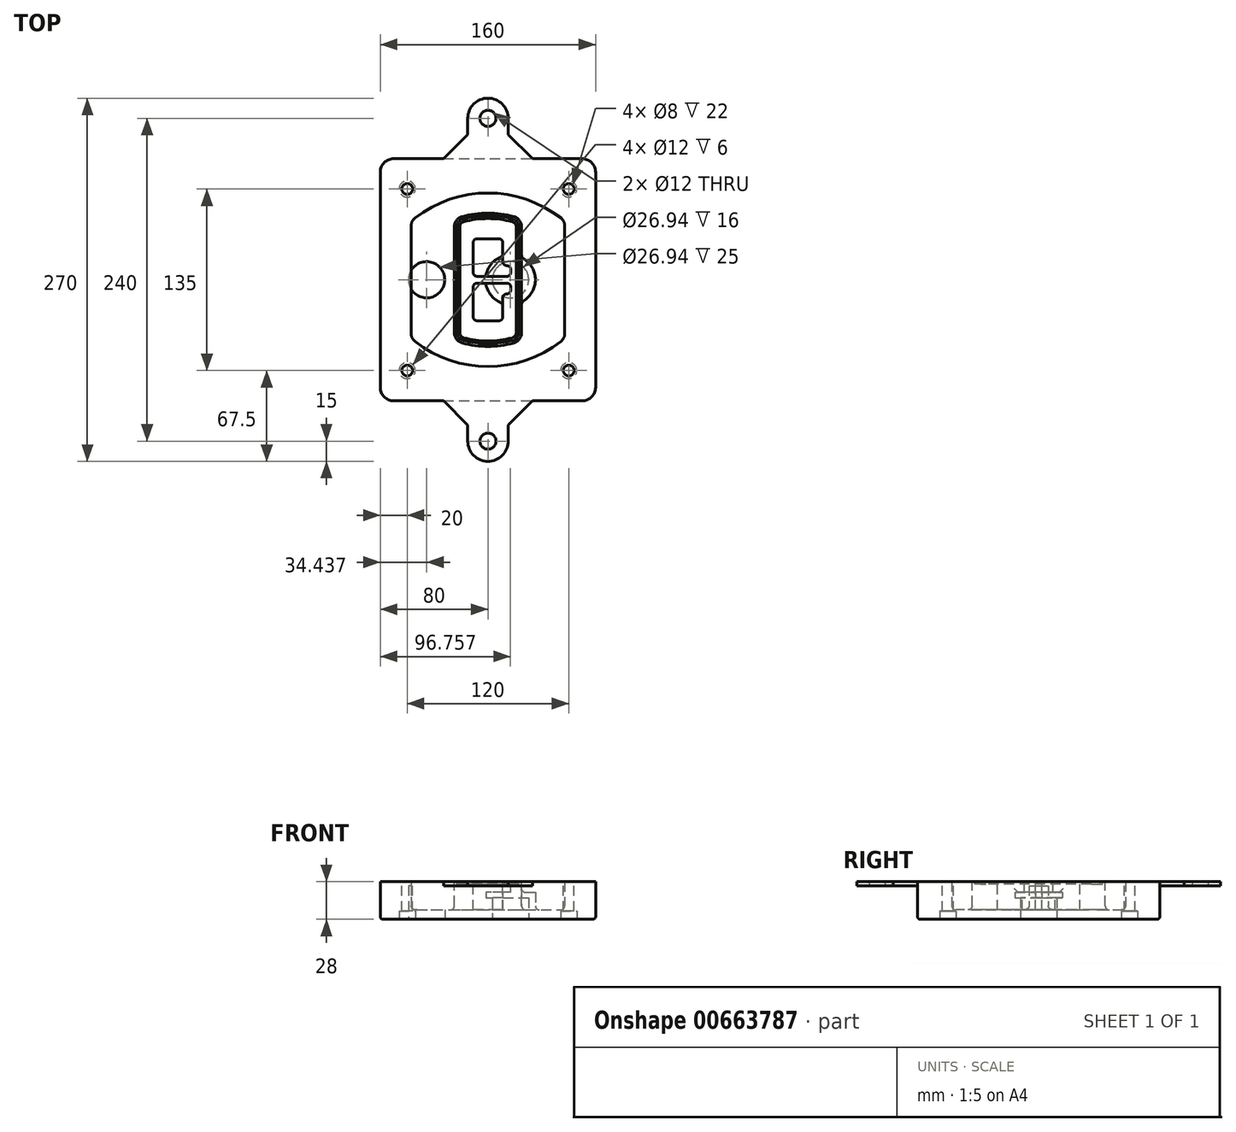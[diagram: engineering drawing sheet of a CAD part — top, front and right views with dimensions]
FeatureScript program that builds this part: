
annotation { "Feature Type Name" : "Feature", "Feature Type Description" : "" }
export const myFeature = defineFeature(function(context is Context, id is Id, definition is map)
    precondition{}
    {
        {
            var Q0;
            Q0=qCreatedBy(makeId("Top.planeOp"),FACE);
            var sketch = newSketch(context, id + "F0", { "sketchPlane" : qUnion([Q0])});
            skPoint(sketch, "E0.rect.middle", {"position": v(0, 0) * mm});
            skLineSegment(sketch, "E1.bottom", {"start": v(-70, -90) * mm, "end": v(70, -90) * mm});
            skLineSegment(sketch, "E1.top", {"start": v(-70, 90) * mm, "end": v(70, 90) * mm});
            skLineSegment(sketch, "E1.left", {"start": v(-80, -80) * mm, "end": v(-80, 80) * mm});
            skLineSegment(sketch, "E1.right", {"start": v(80, -80) * mm, "end": v(80, 80) * mm});
            skLineSegment(sketch, "E2", {"start": v(-80, 90) * mm, "end": v(80, -90) * mm, "construction": true});
            skLineSegment(sketch, "E3", {"start": v(80, 90) * mm, "end": v(-80, -90) * mm, "construction": true});
            skCircle(sketch, "E4", {"center": v(-60, 67.5) * mm, "radius": 4 * mm});
            skCircle(sketch, "E5", {"center": v(60, 67.5) * mm, "radius": 4 * mm});
            skCircle(sketch, "E6", {"center": v(60, -67.5) * mm, "radius": 4 * mm});
            skCircle(sketch, "E7", {"center": v(-60, -67.5) * mm, "radius": 4 * mm});
            skLineSegment(sketch, "E8", {"start": v(-60, 67.5) * mm, "end": v(60, 67.5) * mm, "construction": true});
            skLineSegment(sketch, "E9", {"start": v(60, 67.5) * mm, "end": v(60, -67.5) * mm, "construction": true});
            skLineSegment(sketch, "E10", {"start": v(60, -67.5) * mm, "end": v(-60, -67.5) * mm, "construction": true});
            skLineSegment(sketch, "E11", {"start": v(-60, -67.5) * mm, "end": v(-60, 67.5) * mm, "construction": true});
            skLineSegment(sketch, "E12", {"start": v(-60, 40.3) * mm, "end": v(-60, -40.3) * mm});
            skLineSegment(sketch, "E13", {"start": v(60, 40.3) * mm, "end": v(60, -40.3) * mm});
            skArc(sketch, "E14", {"start": v(56.15, 48.18) * mm, "mid": v(0, 67.5) * mm, "end": v(-56.15, 48.18) * mm});
            skArc(sketch, "E15", {"start": v(-56.15, -48.18) * mm, "mid": v(0, -67.5) * mm, "end": v(56.15, -48.18) * mm});
            skLineSegment(sketch, "E16", {"start": v(-60, 0) * mm, "end": v(60, 0) * mm, "construction": true});
            skPoint(sketch, "E17.visualSharp", {"position": v(-60, -45) * mm});
            skArc(sketch, "E17.filletArc", {"start": v(-60, -40.3) * mm, "mid": v(-58.99, -44.68) * mm, "end": v(-56.15, -48.18) * mm});
            skPoint(sketch, "E18.visualSharp", {"position": v(-60, 45) * mm});
            skArc(sketch, "E18.filletArc", {"start": v(-56.15, 48.18) * mm, "mid": v(-58.99, 44.68) * mm, "end": v(-60, 40.3) * mm});
            skPoint(sketch, "E19.visualSharp", {"position": v(60, 45) * mm});
            skArc(sketch, "E19.filletArc", {"start": v(60, 40.3) * mm, "mid": v(58.99, 44.68) * mm, "end": v(56.15, 48.18) * mm});
            skPoint(sketch, "E20.visualSharp", {"position": v(60, -45) * mm});
            skArc(sketch, "E20.filletArc", {"start": v(56.15, -48.18) * mm, "mid": v(58.99, -44.68) * mm, "end": v(60, -40.3) * mm});
            skPoint(sketch, "E21.visualSharp", {"position": v(-80, 90) * mm});
            skArc(sketch, "E21.filletArc", {"start": v(-70, 90) * mm, "mid": v(-77.07, 87.07) * mm, "end": v(-80, 80) * mm});
            skPoint(sketch, "E22.visualSharp", {"position": v(80, 90) * mm});
            skArc(sketch, "E22.filletArc", {"start": v(80, 80) * mm, "mid": v(77.07, 87.07) * mm, "end": v(70, 90) * mm});
            skPoint(sketch, "E23.visualSharp", {"position": v(80, -90) * mm});
            skArc(sketch, "E23.filletArc", {"start": v(70, -90) * mm, "mid": v(77.07, -87.07) * mm, "end": v(80, -80) * mm});
            skPoint(sketch, "E24.visualSharp", {"position": v(-80, -90) * mm});
            skArc(sketch, "E24.filletArc", {"start": v(-80, -80) * mm, "mid": v(-77.07, -87.07) * mm, "end": v(-70, -90) * mm});
            skArc(sketch, "E25.0", {"start": v(57, 40.3) * mm, "mid": v(56.3, 43.36) * mm, "end": v(54.3, 45.81) * mm});
            skLineSegment(sketch, "E25.1", {"start": v(57, 40.3) * mm, "end": v(57, -40.3) * mm});
            skArc(sketch, "E25.2", {"start": v(54.3, -45.81) * mm, "mid": v(56.3, -43.36) * mm, "end": v(57, -40.3) * mm});
            skArc(sketch, "E25.3", {"start": v(-54.3, -45.81) * mm, "mid": v(0, -64.5) * mm, "end": v(54.3, -45.81) * mm});
            skArc(sketch, "E25.4", {"start": v(-57, -40.3) * mm, "mid": v(-56.3, -43.36) * mm, "end": v(-54.3, -45.81) * mm});
            skArc(sketch, "E25.5", {"start": v(54.3, 45.81) * mm, "mid": v(0, 64.5) * mm, "end": v(-54.3, 45.81) * mm});
            skLineSegment(sketch, "E25.6", {"start": v(-57, 40.3) * mm, "end": v(-57, -40.3) * mm});
            skArc(sketch, "E25.7", {"start": v(-54.3, 45.81) * mm, "mid": v(-56.3, 43.36) * mm, "end": v(-57, 40.3) * mm});
            skArc(sketch, "E26.0", {"start": v(-58.62, 51.33) * mm, "mid": v(-62.58, 46.43) * mm, "end": v(-64, 40.3) * mm});
            skArc(sketch, "E26.1", {"start": v(58.62, 51.33) * mm, "mid": v(0, 71.5) * mm, "end": v(-58.62, 51.33) * mm});
            skArc(sketch, "E26.2", {"start": v(64, 40.3) * mm, "mid": v(62.58, 46.43) * mm, "end": v(58.62, 51.33) * mm});
            skLineSegment(sketch, "E26.3", {"start": v(64, 40.3) * mm, "end": v(64, -40.3) * mm});
            skArc(sketch, "E26.4", {"start": v(58.62, -51.33) * mm, "mid": v(62.58, -46.43) * mm, "end": v(64, -40.3) * mm});
            skLineSegment(sketch, "E26.5", {"start": v(-64, 40.3) * mm, "end": v(-64, -40.3) * mm});
            skArc(sketch, "E26.6", {"start": v(-58.62, -51.33) * mm, "mid": v(0, -71.5) * mm, "end": v(58.62, -51.33) * mm});
            skArc(sketch, "E26.7", {"start": v(-64, -40.3) * mm, "mid": v(-62.58, -46.43) * mm, "end": v(-58.62, -51.33) * mm});
            skSolve(sketch);
        }
        {
            var Q0;
            Q0=makeQuery(id+"F0.imprint","IMPRINT",FACE,{"disambiguationData":[TD([[makeQuery(id+"F0.imprint","IMPRINT",EDGE,{"derivedFrom":sQuery(id+"F0.wireOp",EDGE,"E1.bottom")}),1.0]])]});
            var Q1;
            Q1=makeQuery(id+"F0.imprint","IMPRINT",FACE,{"disambiguationData":[TD([[makeQuery(id+"F0.imprint","IMPRINT",EDGE,{"derivedFrom":sQuery(id+"F0.wireOp",EDGE,"E12")}),1.0]])]});
            var Q2;
            Q2=makeQuery(id+"F0.imprint","IMPRINT",FACE,{"disambiguationData":[TD([[makeQuery(id+"F0.imprint","IMPRINT",EDGE,{"derivedFrom":sQuery(id+"F0.wireOp",EDGE,"E25.0")}),1.0]])]});
            var Q3;
            Q3=makeQuery(id+"F0.imprint","IMPRINT",FACE,{"disambiguationData":[TD([[makeQuery(id+"F0.imprint","IMPRINT",EDGE,{"derivedFrom":sQuery(id+"F0.wireOp",EDGE,"E12")}),-1.0]])]});
            extrude(context, id + "F1", {"entities" : qUnion([Q0, Q1, Q2, Q3]), "oppositeDirection" : true, "depth" : 25 * mm});
        }
        {
            var Q0;
            Q0=makeQuery(id+"F0.imprint","IMPRINT",FACE,{"disambiguationData":[TD([[makeQuery(id+"F0.imprint","IMPRINT",EDGE,{"derivedFrom":sQuery(id+"F0.wireOp",EDGE,"E12")}),1.0]])]});
            extrude(context, id + "F2", {"entities" : qUnion([Q0]), "operationType" : NewBodyOperationType.ADD, "depth" : 3 * mm});
        }
        {
            var Q0;
            Q0=makeQuery(id+"F0.imprint","IMPRINT",FACE,{"disambiguationData":[TD([[makeQuery(id+"F0.imprint","IMPRINT",EDGE,{"derivedFrom":sQuery(id+"F0.wireOp",EDGE,"E25.0")}),1.0]])]});
            extrude(context, id + "F3", {"entities" : qUnion([Q0]), "operationType" : NewBodyOperationType.REMOVE, "oppositeDirection" : true, "depth" : 18 * mm});
        }
        {
            var Q0;
            Q0=makeQuery(id+"F2.opExtrude","CAP_FACE",FACE,{"disambiguationData":[OSD([sQuery(id+"F0.wireOp",EDGE,"E12"),sQuery(id+"F0.wireOp",EDGE,"E13"),sQuery(id+"F0.wireOp",EDGE,"E14"),sQuery(id+"F0.wireOp",EDGE,"E15"),sQuery(id+"F0.wireOp",EDGE,"E17.filletArc"),sQuery(id+"F0.wireOp",EDGE,"E18.filletArc"),sQuery(id+"F0.wireOp",EDGE,"E19.filletArc"),sQuery(id+"F0.wireOp",EDGE,"E20.filletArc"),sQuery(id+"F0.wireOp",EDGE,"E25.0"),sQuery(id+"F0.wireOp",EDGE,"E25.1"),sQuery(id+"F0.wireOp",EDGE,"E25.2"),sQuery(id+"F0.wireOp",EDGE,"E25.3"),sQuery(id+"F0.wireOp",EDGE,"E25.4"),sQuery(id+"F0.wireOp",EDGE,"E25.5"),sQuery(id+"F0.wireOp",EDGE,"E25.6"),sQuery(id+"F0.wireOp",EDGE,"E25.7")])],"isStart":false});
            var sketch = newSketch(context, id + "F4", { "sketchPlane" : qUnion([Q0])});
            skArc(sketch, "E27.0", {"start": v(-19.08, -46.97) * mm, "mid": v(0, -49.5) * mm, "end": v(19.08, -46.97) * mm});
            skArc(sketch, "E28.0", {"start": v(19.08, 46.97) * mm, "mid": v(0, 49.5) * mm, "end": v(-19.08, 46.97) * mm});
            skLineSegment(sketch, "E29", {"start": v(-25, 39.25) * mm, "end": v(-25, -39.25) * mm});
            skLineSegment(sketch, "E30", {"start": v(25, 39.25) * mm, "end": v(25, -39.25) * mm});
            skLineSegment(sketch, "E31", {"start": v(-25, 45.1) * mm, "end": v(25, 45.1) * mm, "construction": true});
            skLineSegment(sketch, "E32", {"start": v(-25, -45.1) * mm, "end": v(25, -45.1) * mm, "construction": true});
            skPoint(sketch, "E33.visualSharp", {"position": v(-25, 45.1) * mm});
            skArc(sketch, "E33.filletArc", {"start": v(-19.08, 46.97) * mm, "mid": v(-23.35, 44.11) * mm, "end": v(-25, 39.25) * mm});
            skPoint(sketch, "E34.visualSharp", {"position": v(25, 45.1) * mm});
            skArc(sketch, "E34.filletArc", {"start": v(25, 39.25) * mm, "mid": v(23.35, 44.11) * mm, "end": v(19.08, 46.97) * mm});
            skPoint(sketch, "E35.visualSharp", {"position": v(25, -45.1) * mm});
            skArc(sketch, "E35.filletArc", {"start": v(19.08, -46.97) * mm, "mid": v(23.35, -44.11) * mm, "end": v(25, -39.25) * mm});
            skPoint(sketch, "E36.visualSharp", {"position": v(-25, -45.1) * mm});
            skArc(sketch, "E36.filletArc", {"start": v(-25, -39.25) * mm, "mid": v(-23.35, -44.11) * mm, "end": v(-19.08, -46.97) * mm});
            skArc(sketch, "E37.0", {"start": v(54.3, 45.81) * mm, "mid": v(0, 64.5) * mm, "end": v(-54.3, 45.81) * mm});
            skArc(sketch, "E37.1", {"start": v(-54.3, 45.81) * mm, "mid": v(-56.3, 43.36) * mm, "end": v(-57, 40.3) * mm});
            skLineSegment(sketch, "E37.2", {"start": v(-57, 40.3) * mm, "end": v(-57, -40.3) * mm});
            skArc(sketch, "E37.3", {"start": v(-57, -40.3) * mm, "mid": v(-56.3, -43.36) * mm, "end": v(-54.3, -45.81) * mm});
            skArc(sketch, "E37.4", {"start": v(-54.3, -45.81) * mm, "mid": v(0, -64.5) * mm, "end": v(54.3, -45.81) * mm});
            skArc(sketch, "E37.5", {"start": v(54.3, -45.81) * mm, "mid": v(56.3, -43.36) * mm, "end": v(57, -40.3) * mm});
            skLineSegment(sketch, "E37.6", {"start": v(57, 40.3) * mm, "end": v(57, -40.3) * mm});
            skArc(sketch, "E37.7", {"start": v(57, 40.3) * mm, "mid": v(56.3, 43.36) * mm, "end": v(54.3, 45.81) * mm});
            skLineSegment(sketch, "E38.0", {"start": v(23, 39.25) * mm, "end": v(23, -39.25) * mm});
            skArc(sketch, "E38.1", {"start": v(18.56, -45.04) * mm, "mid": v(21.76, -42.9) * mm, "end": v(23, -39.25) * mm});
            skArc(sketch, "E38.2", {"start": v(-18.56, -45.04) * mm, "mid": v(0, -47.5) * mm, "end": v(18.56, -45.04) * mm});
            skArc(sketch, "E38.3", {"start": v(-23, -39.25) * mm, "mid": v(-21.76, -42.9) * mm, "end": v(-18.56, -45.04) * mm});
            skLineSegment(sketch, "E38.4", {"start": v(-23, 39.25) * mm, "end": v(-23, -39.25) * mm});
            skArc(sketch, "E38.5", {"start": v(23, 39.25) * mm, "mid": v(21.76, 42.9) * mm, "end": v(18.56, 45.04) * mm});
            skArc(sketch, "E38.6", {"start": v(-18.56, 45.04) * mm, "mid": v(-21.76, 42.9) * mm, "end": v(-23, 39.25) * mm});
            skArc(sketch, "E38.7", {"start": v(18.56, 45.04) * mm, "mid": v(0, 47.5) * mm, "end": v(-18.56, 45.04) * mm});
            skArc(sketch, "E39.0", {"start": v(21, 39.25) * mm, "mid": v(20.18, 41.68) * mm, "end": v(18.04, 43.1) * mm});
            skLineSegment(sketch, "E39.1", {"start": v(21, 39.25) * mm, "end": v(21, -39.25) * mm});
            skArc(sketch, "E39.2", {"start": v(18.04, -43.1) * mm, "mid": v(20.18, -41.68) * mm, "end": v(21, -39.25) * mm});
            skArc(sketch, "E39.3", {"start": v(-18.04, -43.1) * mm, "mid": v(0, -45.5) * mm, "end": v(18.04, -43.1) * mm});
            skArc(sketch, "E39.4", {"start": v(-21, -39.25) * mm, "mid": v(-20.18, -41.68) * mm, "end": v(-18.04, -43.1) * mm});
            skArc(sketch, "E39.5", {"start": v(18.04, 43.1) * mm, "mid": v(0, 45.5) * mm, "end": v(-18.04, 43.1) * mm});
            skLineSegment(sketch, "E39.6", {"start": v(-21, 39.25) * mm, "end": v(-21, -39.25) * mm});
            skArc(sketch, "E39.7", {"start": v(-18.04, 43.1) * mm, "mid": v(-20.18, 41.68) * mm, "end": v(-21, 39.25) * mm});
            skLineSegment(sketch, "E40", {"start": v(-25, 0) * mm, "end": v(25, 0) * mm, "construction": true});
            skLineSegment(sketch, "E41", {"start": v(-11, 5.5) * mm, "end": v(-11, 27.5) * mm});
            skLineSegment(sketch, "E42", {"start": v(-8, 30.5) * mm, "end": v(8, 30.5) * mm});
            skLineSegment(sketch, "E43", {"start": v(11, 27.5) * mm, "end": v(11, 13.5) * mm});
            skLineSegment(sketch, "E44", {"start": v(14, 10.5) * mm, "end": v(14, 10.5) * mm});
            skLineSegment(sketch, "E45", {"start": v(17, 7.5) * mm, "end": v(17, 5.5) * mm});
            skLineSegment(sketch, "E46", {"start": v(14, 2.5) * mm, "end": v(-8, 2.5) * mm});
            skPoint(sketch, "E47.visualSharp", {"position": v(-11, 30.5) * mm});
            skArc(sketch, "E47.filletArc", {"start": v(-8, 30.5) * mm, "mid": v(-10.12, 29.62) * mm, "end": v(-11, 27.5) * mm});
            skPoint(sketch, "E48.visualSharp", {"position": v(11, 30.5) * mm});
            skArc(sketch, "E48.filletArc", {"start": v(11, 27.5) * mm, "mid": v(10.12, 29.62) * mm, "end": v(8, 30.5) * mm});
            skPoint(sketch, "E49.visualSharp", {"position": v(11, 10.5) * mm});
            skArc(sketch, "E49.filletArc", {"start": v(11, 13.5) * mm, "mid": v(11.88, 11.38) * mm, "end": v(14, 10.5) * mm});
            skPoint(sketch, "E50.visualSharp", {"position": v(17, 10.5) * mm});
            skArc(sketch, "E50.filletArc", {"start": v(17, 7.5) * mm, "mid": v(16.12, 9.62) * mm, "end": v(14, 10.5) * mm});
            skPoint(sketch, "E51.visualSharp", {"position": v(17, 2.5) * mm});
            skArc(sketch, "E51.filletArc", {"start": v(14, 2.5) * mm, "mid": v(16.12, 3.38) * mm, "end": v(17, 5.5) * mm});
            skPoint(sketch, "E52.visualSharp", {"position": v(-11, 2.5) * mm});
            skArc(sketch, "E52.filletArc", {"start": v(-11, 5.5) * mm, "mid": v(-10.12, 3.38) * mm, "end": v(-8, 2.5) * mm});
            skLineSegment(sketch, "E53.0.MirrorCS", {"start": v(14, -2.5) * mm, "end": v(-8, -2.5) * mm});
            skArc(sketch, "E54.0.MirrorCS", {"start": v(-11, -5.5) * mm, "mid": v(-10.12, -3.38) * mm, "end": v(-8, -2.5) * mm});
            skLineSegment(sketch, "E55.0.MirrorCS", {"start": v(-11, -5.5) * mm, "end": v(-11, -27.5) * mm});
            skArc(sketch, "E56.0.MirrorCS", {"start": v(-8, -30.5) * mm, "mid": v(-10.12, -29.62) * mm, "end": v(-11, -27.5) * mm});
            skLineSegment(sketch, "E57.0.MirrorCS", {"start": v(-8, -30.5) * mm, "end": v(8, -30.5) * mm});
            skArc(sketch, "E58.0.MirrorCS", {"start": v(11, -27.5) * mm, "mid": v(10.12, -29.62) * mm, "end": v(8, -30.5) * mm});
            skLineSegment(sketch, "E59.0.MirrorCS", {"start": v(11, -27.5) * mm, "end": v(11, -13.5) * mm});
            skArc(sketch, "E60.0.MirrorCS", {"start": v(11, -13.5) * mm, "mid": v(11.88, -11.38) * mm, "end": v(14, -10.5) * mm});
            skArc(sketch, "E61.0.MirrorCS", {"start": v(17, -7.5) * mm, "mid": v(16.12, -9.62) * mm, "end": v(14, -10.5) * mm});
            skLineSegment(sketch, "E62.0.MirrorCS", {"start": v(17, -7.5) * mm, "end": v(17, -5.5) * mm});
            skArc(sketch, "E63.0.MirrorCS", {"start": v(14, -2.5) * mm, "mid": v(16.12, -3.38) * mm, "end": v(17, -5.5) * mm});
            skSolve(sketch);
        }
        {
            var Q0;
            Q0=makeQuery(id+"F4.imprint","IMPRINT",FACE,{"disambiguationData":[TD([[makeQuery(id+"F4.imprint","IMPRINT",EDGE,{"derivedFrom":sQuery(id+"F4.wireOp",EDGE,"E27.0")}),1.0]])]});
            var Q1;
            Q1=makeQuery(id+"F4.imprint","IMPRINT",FACE,{"disambiguationData":[TD([[makeQuery(id+"F4.imprint","IMPRINT",EDGE,{"derivedFrom":sQuery(id+"F4.wireOp",EDGE,"E38.0")}),-1.0]])]});
            var Q2;
            Q2=makeQuery(id+"F4.imprint","IMPRINT",FACE,{"disambiguationData":[TD([[makeQuery(id+"F4.imprint","IMPRINT",EDGE,{"derivedFrom":sQuery(id+"F4.wireOp",EDGE,"E39.0")}),1.0]])]});
            extrude(context, id + "F5", {"entities" : qUnion([Q0, Q1, Q2]), "operationType" : NewBodyOperationType.ADD, "endBound" : BoundingType.UP_TO_NEXT, "oppositeDirection" : true, "depth" : 25 * mm});
        }
        {
            var Q0;
            Q0=makeQuery(id+"F4.imprint","IMPRINT",FACE,{"disambiguationData":[TD([[makeQuery(id+"F4.imprint","IMPRINT",EDGE,{"derivedFrom":sQuery(id+"F4.wireOp",EDGE,"E38.0")}),-1.0]])]});
            extrude(context, id + "F6", {"entities" : qUnion([Q0]), "operationType" : NewBodyOperationType.REMOVE, "oppositeDirection" : true, "depth" : 2 * mm});
        }
        {
            var Q0;
            Q0=makeQuery(id+"F1.opExtrude","CAP_FACE",FACE,{"disambiguationData":[OSD([sQuery(id+"F0.wireOp",EDGE,"E1.bottom"),sQuery(id+"F0.wireOp",EDGE,"E1.top"),sQuery(id+"F0.wireOp",EDGE,"E1.left"),sQuery(id+"F0.wireOp",EDGE,"E1.right"),sQuery(id+"F0.wireOp",EDGE,"E4"),sQuery(id+"F0.wireOp",EDGE,"E5"),sQuery(id+"F0.wireOp",EDGE,"E6"),sQuery(id+"F0.wireOp",EDGE,"E7"),sQuery(id+"F0.wireOp",EDGE,"E21.filletArc"),sQuery(id+"F0.wireOp",EDGE,"E22.filletArc"),sQuery(id+"F0.wireOp",EDGE,"E23.filletArc"),sQuery(id+"F0.wireOp",EDGE,"E24.filletArc")])],"isStart":false});
            var sketch = newSketch(context, id + "F7", { "sketchPlane" : qUnion([Q0])});
            skCircle(sketch, "E64", {"center": v(16.76, 0) * mm, "radius": 13.47 * mm});
            skCircle(sketch, "E65", {"center": v(-45.56, 0) * mm, "radius": 13.47 * mm});
            skLineSegment(sketch, "E66", {"start": v(80, 0) * mm, "end": v(-80, 0) * mm});
            skCircle(sketch, "E67", {"center": v(16.76, 0) * mm, "radius": 18.47 * mm});
            skCircle(sketch, "E68", {"center": v(60, -67.5) * mm, "radius": 6 * mm});
            skCircle(sketch, "E69", {"center": v(-60, -67.5) * mm, "radius": 6 * mm});
            skCircle(sketch, "E70", {"center": v(-60, 67.5) * mm, "radius": 6 * mm});
            skCircle(sketch, "E71", {"center": v(60, 67.5) * mm, "radius": 6 * mm});
            skSolve(sketch);
        }
        {
            var Q0;
            {var subQ1=sQuery(id+"F7.wireOp",EDGE,"E66");var subQ4=sQuery(id+"F7.wireOp",EDGE,"E64");var subQ6=makeQuery(id+"F7.imprint","INTERSECT",VERTEX,{"disambiguationData":[OD(0.0)],"derivedFrom":[subQ4,subQ1]});Q0=makeQuery(id+"F7.imprint","IMPRINT",FACE,{"disambiguationData":[TD([[makeQuery(id+"F7.imprint","IMPRINT",EDGE,{"disambiguationData":[TD([[subQ6,-1.0]])],"derivedFrom":subQ4}),-1.0]])]});}
            var Q1;
            {var subQ0=sQuery(id+"F7.wireOp",EDGE,"E66");var subQ1=sQuery(id+"F7.wireOp",EDGE,"E64");var subQ3=makeQuery(id+"F7.imprint","INTERSECT",VERTEX,{"disambiguationData":[OD(0.0)],"derivedFrom":[subQ1,subQ0]});Q1=makeQuery(id+"F7.imprint","IMPRINT",FACE,{"disambiguationData":[TD([[makeQuery(id+"F7.imprint","IMPRINT",EDGE,{"disambiguationData":[TD([[subQ3,-1.0]])],"derivedFrom":subQ1}),1.0]])]});}
            var Q2;
            {var subQ0=sQuery(id+"F7.wireOp",EDGE,"E66");var subQ1=sQuery(id+"F7.wireOp",EDGE,"E64");var subQ3=makeQuery(id+"F7.imprint","INTERSECT",VERTEX,{"disambiguationData":[OD(0.0)],"derivedFrom":[subQ1,subQ0]});Q2=makeQuery(id+"F7.imprint","IMPRINT",FACE,{"disambiguationData":[TD([[makeQuery(id+"F7.imprint","IMPRINT",EDGE,{"disambiguationData":[TD([[subQ3,1.0]])],"derivedFrom":subQ1}),1.0]])]});}
            var Q3;
            {var subQ1=sQuery(id+"F7.wireOp",EDGE,"E66");var subQ4=sQuery(id+"F7.wireOp",EDGE,"E64");var subQ6=makeQuery(id+"F7.imprint","INTERSECT",VERTEX,{"disambiguationData":[OD(0.0)],"derivedFrom":[subQ4,subQ1]});Q3=makeQuery(id+"F7.imprint","IMPRINT",FACE,{"disambiguationData":[TD([[makeQuery(id+"F7.imprint","IMPRINT",EDGE,{"disambiguationData":[TD([[subQ6,1.0]])],"derivedFrom":subQ4}),-1.0]])]});}
            extrude(context, id + "F8", {"entities" : qUnion([Q0, Q1, Q2, Q3]), "operationType" : NewBodyOperationType.ADD, "oppositeDirection" : true, "depth" : 20 * mm});
        }
        {
            var Q0;
            {var subQ0=sQuery(id+"F7.wireOp",EDGE,"E66");var subQ1=sQuery(id+"F7.wireOp",EDGE,"E64");var subQ3=makeQuery(id+"F7.imprint","INTERSECT",VERTEX,{"disambiguationData":[OD(0.0)],"derivedFrom":[subQ1,subQ0]});Q0=makeQuery(id+"F7.imprint","IMPRINT",FACE,{"disambiguationData":[TD([[makeQuery(id+"F7.imprint","IMPRINT",EDGE,{"disambiguationData":[TD([[subQ3,-1.0]])],"derivedFrom":subQ1}),1.0]])]});}
            var Q1;
            {var subQ0=sQuery(id+"F7.wireOp",EDGE,"E66");var subQ1=sQuery(id+"F7.wireOp",EDGE,"E64");var subQ3=makeQuery(id+"F7.imprint","INTERSECT",VERTEX,{"disambiguationData":[OD(0.0)],"derivedFrom":[subQ1,subQ0]});Q1=makeQuery(id+"F7.imprint","IMPRINT",FACE,{"disambiguationData":[TD([[makeQuery(id+"F7.imprint","IMPRINT",EDGE,{"disambiguationData":[TD([[subQ3,1.0]])],"derivedFrom":subQ1}),1.0]])]});}
            extrude(context, id + "F9", {"entities" : qUnion([Q0, Q1]), "operationType" : NewBodyOperationType.REMOVE, "oppositeDirection" : true, "depth" : 16 * mm});
        }
        {
            var Q0;
            {var subQ0=sQuery(id+"F7.wireOp",EDGE,"E66");var subQ1=sQuery(id+"F7.wireOp",EDGE,"E65");var subQ3=makeQuery(id+"F7.imprint","INTERSECT",VERTEX,{"disambiguationData":[OD(0.0)],"derivedFrom":[subQ1,subQ0]});Q0=makeQuery(id+"F7.imprint","IMPRINT",FACE,{"disambiguationData":[TD([[makeQuery(id+"F7.imprint","IMPRINT",EDGE,{"disambiguationData":[TD([[subQ3,-1.0]])],"derivedFrom":subQ1}),1.0]])]});}
            var Q1;
            {var subQ0=sQuery(id+"F7.wireOp",EDGE,"E66");var subQ1=sQuery(id+"F7.wireOp",EDGE,"E65");var subQ3=makeQuery(id+"F7.imprint","INTERSECT",VERTEX,{"disambiguationData":[OD(0.0)],"derivedFrom":[subQ1,subQ0]});Q1=makeQuery(id+"F7.imprint","IMPRINT",FACE,{"disambiguationData":[TD([[makeQuery(id+"F7.imprint","IMPRINT",EDGE,{"disambiguationData":[TD([[subQ3,1.0]])],"derivedFrom":subQ1}),1.0]])]});}
            extrude(context, id + "F10", {"entities" : qUnion([Q0, Q1]), "operationType" : NewBodyOperationType.REMOVE, "oppositeDirection" : true, "depth" : 25 * mm});
        }
        {
            var Q0;
            Q0=makeQuery(id+"F7.imprint","IMPRINT",FACE,{"disambiguationData":[TD([[makeQuery(id+"F7.imprint","IMPRINT",EDGE,{"derivedFrom":sQuery(id+"F7.wireOp",EDGE,"E68")}),1.0]])]});
            var Q1;
            Q1=makeQuery(id+"F7.imprint","IMPRINT",FACE,{"disambiguationData":[TD([[makeQuery(id+"F7.imprint","IMPRINT",EDGE,{"derivedFrom":makeQuery(id+"F1.opExtrude","CAP_EDGE",EDGE,{"disambiguationData":[OSD([sQuery(id+"F0.wireOp",EDGE,"E5")])],"isStart":false})}),-1.0]])]});
            var Q2;
            Q2=makeQuery(id+"F7.imprint","IMPRINT",FACE,{"disambiguationData":[TD([[makeQuery(id+"F7.imprint","IMPRINT",EDGE,{"derivedFrom":sQuery(id+"F7.wireOp",EDGE,"E69")}),1.0]])]});
            var Q3;
            Q3=makeQuery(id+"F7.imprint","IMPRINT",FACE,{"disambiguationData":[TD([[makeQuery(id+"F7.imprint","IMPRINT",EDGE,{"derivedFrom":makeQuery(id+"F1.opExtrude","CAP_EDGE",EDGE,{"disambiguationData":[OSD([sQuery(id+"F0.wireOp",EDGE,"E4")])],"isStart":false})}),-1.0]])]});
            var Q4;
            Q4=makeQuery(id+"F7.imprint","IMPRINT",FACE,{"disambiguationData":[TD([[makeQuery(id+"F7.imprint","IMPRINT",EDGE,{"derivedFrom":sQuery(id+"F7.wireOp",EDGE,"E70")}),1.0]])]});
            var Q5;
            Q5=makeQuery(id+"F7.imprint","IMPRINT",FACE,{"disambiguationData":[TD([[makeQuery(id+"F7.imprint","IMPRINT",EDGE,{"derivedFrom":makeQuery(id+"F1.opExtrude","CAP_EDGE",EDGE,{"disambiguationData":[OSD([sQuery(id+"F0.wireOp",EDGE,"E7")])],"isStart":false})}),-1.0]])]});
            var Q6;
            Q6=makeQuery(id+"F7.imprint","IMPRINT",FACE,{"disambiguationData":[TD([[makeQuery(id+"F7.imprint","IMPRINT",EDGE,{"derivedFrom":sQuery(id+"F7.wireOp",EDGE,"E71")}),1.0]])]});
            var Q7;
            Q7=makeQuery(id+"F7.imprint","IMPRINT",FACE,{"disambiguationData":[TD([[makeQuery(id+"F7.imprint","IMPRINT",EDGE,{"derivedFrom":makeQuery(id+"F1.opExtrude","CAP_EDGE",EDGE,{"disambiguationData":[OSD([sQuery(id+"F0.wireOp",EDGE,"E6")])],"isStart":false})}),-1.0]])]});
            extrude(context, id + "F11", {"entities" : qUnion([Q0, Q1, Q2, Q3, Q4, Q5, Q6, Q7]), "operationType" : NewBodyOperationType.REMOVE, "oppositeDirection" : true, "depth" : 6 * mm});
        }
        {
            var Q0;
            Q0=makeQuery(id+"F9.boolean.opBoolean","COPY",FACE,{"derivedFrom":makeQuery(id+"F9.opExtrude","CAP_FACE",FACE,{"disambiguationData":[OSD([sQuery(id+"F7.wireOp",EDGE,"E64")])],"isStart":false})});
            var sketch = newSketch(context, id + "F12", { "sketchPlane" : qUnion([Q0])});
            skArc(sketch, "E72.0", {"start": v(11, 17.55) * mm, "mid": v(2.57, 11.82) * mm, "end": v(-1.54, 2.5) * mm});
            skArc(sketch, "E72.1", {"start": v(-1.54, -2.5) * mm, "mid": v(2.57, -11.82) * mm, "end": v(11, -17.55) * mm});
            skLineSegment(sketch, "E73", {"start": v(-1.54, -2.5) * mm, "end": v(14, -2.5) * mm});
            skLineSegment(sketch, "E74.0", {"start": v(14, 2.5) * mm, "end": v(-1.54, 2.5) * mm});
            skArc(sketch, "E74.1", {"start": v(14, 2.5) * mm, "mid": v(16.12, 3.38) * mm, "end": v(17, 5.5) * mm});
            skLineSegment(sketch, "E74.2", {"start": v(17, 7.5) * mm, "end": v(17, 5.5) * mm});
            skArc(sketch, "E74.3", {"start": v(17, 7.5) * mm, "mid": v(16.12, 9.62) * mm, "end": v(14, 10.5) * mm});
            skArc(sketch, "E74.4", {"start": v(11, 13.5) * mm, "mid": v(11.88, 11.38) * mm, "end": v(14, 10.5) * mm});
            skLineSegment(sketch, "E74.5", {"start": v(11, 17.55) * mm, "end": v(11, 13.5) * mm});
            skLineSegment(sketch, "E74.7", {"start": v(14, -2.5) * mm, "end": v(-1.54, -2.5) * mm});
            skArc(sketch, "E74.8", {"start": v(14, -2.5) * mm, "mid": v(16.12, -3.38) * mm, "end": v(17, -5.5) * mm});
            skLineSegment(sketch, "E74.9", {"start": v(17, -7.5) * mm, "end": v(17, -5.5) * mm});
            skArc(sketch, "E74.10", {"start": v(17, -7.5) * mm, "mid": v(16.12, -9.62) * mm, "end": v(14, -10.5) * mm});
            skArc(sketch, "E74.11", {"start": v(11, -13.5) * mm, "mid": v(11.88, -11.38) * mm, "end": v(14, -10.5) * mm});
            skLineSegment(sketch, "E74.12", {"start": v(11, -17.55) * mm, "end": v(11, -13.5) * mm});
            skPoint(sketch, "E75.orphan", {"position": v(11, -27.5) * mm});
            skPoint(sketch, "E76.orphan", {"position": v(-8, -2.5) * mm});
            skPoint(sketch, "E77.orphan", {"position": v(-8, 2.5) * mm});
            skPoint(sketch, "E78.orphan", {"position": v(11, 27.5) * mm});
            skSolve(sketch);
        }
        {
            var Q0;
            {var subQ7=sQuery(id+"F12.wireOp",EDGE,"E72.0");var subQ14=sQuery(id+"F12.wireOp",EDGE,"E72.1");var subQ16=sQuery(id+"F12.wireOp",EDGE,"E74.1");var subQ18=sQuery(id+"F12.wireOp",EDGE,"E74.8");Q0=qUnion([makeQuery(id+"F12.imprint","IMPRINT",FACE,{"disambiguationData":[TD([[makeQuery(id+"F12.imprint","IMPRINT",EDGE,{"derivedFrom":subQ7}),1.0]])]}),makeQuery(id+"F12.imprint","IMPRINT",FACE,{"disambiguationData":[TD([[makeQuery(id+"F12.imprint","IMPRINT",EDGE,{"derivedFrom":subQ14}),1.0]])]}),makeQuery(id+"F12.imprint","IMPRINT",FACE,{"disambiguationData":[TD([[makeQuery(id+"F12.imprint","IMPRINT",EDGE,{"derivedFrom":subQ16}),1.0]])]}),makeQuery(id+"F12.imprint","IMPRINT",FACE,{"disambiguationData":[TD([[makeQuery(id+"F12.imprint","IMPRINT",EDGE,{"derivedFrom":subQ18}),-1.0]])]})]);}
            var Q1;
            Q1=makeQuery(id+"F5.boolean.opBoolean","SPLIT",FACE,{"disambiguationData":[TD([makeQuery(id+"F5.opExtrude","SWEPT_FACE",FACE,{"disambiguationData":[OSD([sQuery(id+"F4.wireOp",EDGE,"E41")])]})])],"derivedFrom":makeQuery(id+"F3.boolean.opBoolean","COPY",FACE,{"derivedFrom":makeQuery(id+"F3.opExtrude","CAP_FACE",FACE,{"disambiguationData":[OSD([sQuery(id+"F0.wireOp",EDGE,"E25.0"),sQuery(id+"F0.wireOp",EDGE,"E25.1"),sQuery(id+"F0.wireOp",EDGE,"E25.2"),sQuery(id+"F0.wireOp",EDGE,"E25.3"),sQuery(id+"F0.wireOp",EDGE,"E25.4"),sQuery(id+"F0.wireOp",EDGE,"E25.5"),sQuery(id+"F0.wireOp",EDGE,"E25.6"),sQuery(id+"F0.wireOp",EDGE,"E25.7")])],"isStart":false})})});
            extrude(context, id + "F13", {"entities" : qUnion([Q0]), "operationType" : NewBodyOperationType.REMOVE, "endBound" : BoundingType.UP_TO_SURFACE, "endBoundEntityFace" : qUnion([Q1]), "depth" : 25 * mm});
        }
        {
            var Q0;
            Q0=makeQuery(id+"F3.boolean.opBoolean","COPY",EDGE,{"derivedFrom":makeQuery(id+"F3.opExtrude","CAP_EDGE",EDGE,{"disambiguationData":[OSD([sQuery(id+"F0.wireOp",EDGE,"E25.6")])],"isStart":false})});
            var Q1;
            Q1=makeQuery(id+"F8.boolean.opBoolean","INTERSECT",EDGE,{"derivedFrom":[makeQuery(id+"F5.opExtrude","SWEPT_FACE",FACE,{"disambiguationData":[OSD([sQuery(id+"F4.wireOp",EDGE,"E30")])]}),makeQuery(id+"F8.opExtrude","CAP_FACE",FACE,{"disambiguationData":[OSD([sQuery(id+"F7.wireOp",EDGE,"E67")])],"isStart":false})]});
            var Q2;
            Q2=makeQuery(id+"F8.boolean.opBoolean","INTERSECT",EDGE,{"disambiguationData":[OD(1.0)],"derivedFrom":[makeQuery(id+"F5.opExtrude","SWEPT_FACE",FACE,{"disambiguationData":[OSD([sQuery(id+"F4.wireOp",EDGE,"E30")])]}),makeQuery(id+"F8.opExtrude","SWEPT_FACE",FACE,{"disambiguationData":[OSD([sQuery(id+"F7.wireOp",EDGE,"E67")])]})]});
            var Q3;
            {var subQ0=sQuery(id+"F4.wireOp",EDGE,"E30");Q3=makeQuery(id+"F8.boolean.opBoolean","SPLIT",EDGE,{"disambiguationData":[TD([makeQuery(id+"F5.opExtrude","SWEPT_FACE",FACE,{"disambiguationData":[OSD([sQuery(id+"F4.wireOp",EDGE,"E35.filletArc")])]})])],"derivedFrom":makeQuery(id+"F5.opExtrude","CAP_EDGE",EDGE,{"disambiguationData":[OSD([subQ0])],"isStart":false})});}
            var Q4;
            {var subQ0=sQuery(id+"F0.wireOp",EDGE,"E25.7");var subQ1=sQuery(id+"F0.wireOp",EDGE,"E25.1");var subQ2=sQuery(id+"F0.wireOp",EDGE,"E25.6");var subQ3=sQuery(id+"F0.wireOp",EDGE,"E25.5");var subQ4=sQuery(id+"F0.wireOp",EDGE,"E25.4");var subQ5=sQuery(id+"F0.wireOp",EDGE,"E25.0");var subQ6=sQuery(id+"F0.wireOp",EDGE,"E25.2");var subQ7=sQuery(id+"F0.wireOp",EDGE,"E25.3");Q4=makeQuery(id+"F8.boolean.opBoolean","INTERSECT",EDGE,{"derivedFrom":[makeQuery(id+"F5.boolean.opBoolean","SPLIT",FACE,{"disambiguationData":[TD([makeQuery(id+"F2.opExtrude","SWEPT_FACE",FACE,{"disambiguationData":[OSD([subQ5])]})])],"derivedFrom":makeQuery(id+"F3.boolean.opBoolean","COPY",FACE,{"derivedFrom":makeQuery(id+"F3.opExtrude","CAP_FACE",FACE,{"disambiguationData":[OSD([subQ5,subQ1,subQ6,subQ7,subQ4,subQ3,subQ2,subQ0])],"isStart":false})})}),makeQuery(id+"F8.opExtrude","SWEPT_FACE",FACE,{"disambiguationData":[OSD([sQuery(id+"F7.wireOp",EDGE,"E67")])]})]});}
            var Q5;
            Q5=makeQuery(id+"F8.boolean.opBoolean","INTERSECT",EDGE,{"disambiguationData":[OD(0.0)],"derivedFrom":[makeQuery(id+"F5.opExtrude","SWEPT_FACE",FACE,{"disambiguationData":[OSD([sQuery(id+"F4.wireOp",EDGE,"E30")])]}),makeQuery(id+"F8.opExtrude","SWEPT_FACE",FACE,{"disambiguationData":[OSD([sQuery(id+"F7.wireOp",EDGE,"E67")])]})]});
            fillet(context, id + "F14", {"entities" : qUnion([Q0, Q1, Q2, Q3, Q4, Q5]), "radius" : 3 * mm, "tangentPropagation" : true, "allowEdgeOverflow" : false});
        }
        {
            var Q0;
            Q0=makeQuery(id+"F1.opExtrude","CAP_EDGE",EDGE,{"disambiguationData":[OSD([sQuery(id+"F0.wireOp",EDGE,"E1.bottom")])],"isStart":false});
            fillet(context, id + "F15", {"entities" : qUnion([Q0]), "radius" : 2 * mm, "tangentPropagation" : true, "allowEdgeOverflow" : false});
        }
        {
            var Q0;
            {var subQ0=sQuery(id+"F0.wireOp",EDGE,"E21.filletArc");var subQ1=sQuery(id+"F0.wireOp",EDGE,"E7");var subQ2=sQuery(id+"F0.wireOp",EDGE,"E6");var subQ3=sQuery(id+"F0.wireOp",EDGE,"E5");var subQ4=sQuery(id+"F0.wireOp",EDGE,"E4");var subQ5=sQuery(id+"F0.wireOp",EDGE,"E22.filletArc");var subQ6=sQuery(id+"F0.wireOp",EDGE,"E1.bottom");var subQ7=sQuery(id+"F0.wireOp",EDGE,"E1.right");var subQ8=sQuery(id+"F0.wireOp",EDGE,"E1.top");var subQ9=sQuery(id+"F0.wireOp",EDGE,"E1.left");var subQ10=sQuery(id+"F0.wireOp",EDGE,"E23.filletArc");var subQ11=sQuery(id+"F0.wireOp",EDGE,"E24.filletArc");Q0=makeQuery(id+"F2.boolean.opBoolean","SPLIT",FACE,{"disambiguationData":[TD([makeQuery(id+"F1.opExtrude","SWEPT_FACE",FACE,{"disambiguationData":[OSD([subQ6])]})])],"derivedFrom":makeQuery(id+"F1.opExtrude","CAP_FACE",FACE,{"disambiguationData":[OSD([subQ6,subQ8,subQ9,subQ7,subQ4,subQ3,subQ2,subQ1,subQ0,subQ5,subQ10,subQ11])],"isStart":true})});}
            var sketch = newSketch(context, id + "F16", { "sketchPlane" : qUnion([Q0])});
            skLineSegment(sketch, "E79", {"start": v(0, 90) * mm, "end": v(0, 120) * mm, "construction": true});
            skCircle(sketch, "E80", {"center": v(0, 120) * mm, "radius": 6 * mm});
            skArc(sketch, "E81", {"start": v(15, 120) * mm, "mid": v(0, 135) * mm, "end": v(-15, 120) * mm});
            skLineSegment(sketch, "E82", {"start": v(-15, 120) * mm, "end": v(-15, 108) * mm});
            skLineSegment(sketch, "E83", {"start": v(15, 120) * mm, "end": v(15, 108) * mm});
            skLineSegment(sketch, "E84", {"start": v(15, 108) * mm, "end": v(33, 90) * mm});
            skLineSegment(sketch, "E85", {"start": v(-15, 108) * mm, "end": v(-33, 90) * mm});
            skPoint(sketch, "E86.startSnap0", {"position": v(0, -90) * mm});
            skLineSegment(sketch, "E87", {"start": v(0, 0) * mm, "end": v(38.33, 0) * mm});
            skLineSegment(sketch, "E88.MirrorCS", {"start": v(0, -90) * mm, "end": v(0, -120) * mm, "construction": true});
            skLineSegment(sketch, "E89.MirrorCS", {"start": v(15, -108) * mm, "end": v(33, -90) * mm});
            skLineSegment(sketch, "E90.MirrorCS", {"start": v(15, -120) * mm, "end": v(15, -108) * mm});
            skArc(sketch, "E91.MirrorCS", {"start": v(15, -120) * mm, "mid": v(0, -135) * mm, "end": v(-15, -120) * mm});
            skLineSegment(sketch, "E92.MirrorCS", {"start": v(-15, -120) * mm, "end": v(-15, -108) * mm});
            skLineSegment(sketch, "E93.MirrorCS", {"start": v(-15, -108) * mm, "end": v(-33, -90) * mm});
            skCircle(sketch, "E94.MirrorC", {"center": v(0, -120) * mm, "radius": 6 * mm});
            skSolve(sketch);
        }
        {
            var Q0;
            {var subQ0=sQuery(id+"F16.wireOp",EDGE,"E89.MirrorCS");Q0=makeQuery(id+"F16.imprint","IMPRINT",FACE,{"disambiguationData":[TD([[makeQuery(id+"F16.imprint","IMPRINT",EDGE,{"derivedFrom":subQ0}),1.0]])]});}
            var Q1;
            Q1=makeQuery(id+"F16.imprint","IMPRINT",FACE,{"disambiguationData":[TD([[makeQuery(id+"F16.imprint","IMPRINT",EDGE,{"derivedFrom":makeQuery(id+"F1.opExtrude","CAP_EDGE",EDGE,{"disambiguationData":[OSD([sQuery(id+"F0.wireOp",EDGE,"E1.left")])],"isStart":true})}),-1.0]])]});
            var Q2;
            Q2=makeQuery(id+"F16.imprint","IMPRINT",FACE,{"disambiguationData":[TD([[makeQuery(id+"F16.imprint","IMPRINT",EDGE,{"derivedFrom":sQuery(id+"F16.wireOp",EDGE,"E80")}),-1.0]])]});
            var Q3;
            Q3=makeQuery(id+"F2.opExtrude","CAP_FACE",FACE,{"disambiguationData":[OSD([sQuery(id+"F0.wireOp",EDGE,"E12"),sQuery(id+"F0.wireOp",EDGE,"E13"),sQuery(id+"F0.wireOp",EDGE,"E14"),sQuery(id+"F0.wireOp",EDGE,"E15"),sQuery(id+"F0.wireOp",EDGE,"E17.filletArc"),sQuery(id+"F0.wireOp",EDGE,"E18.filletArc"),sQuery(id+"F0.wireOp",EDGE,"E19.filletArc"),sQuery(id+"F0.wireOp",EDGE,"E20.filletArc"),sQuery(id+"F0.wireOp",EDGE,"E25.0"),sQuery(id+"F0.wireOp",EDGE,"E25.1"),sQuery(id+"F0.wireOp",EDGE,"E25.2"),sQuery(id+"F0.wireOp",EDGE,"E25.3"),sQuery(id+"F0.wireOp",EDGE,"E25.4"),sQuery(id+"F0.wireOp",EDGE,"E25.5"),sQuery(id+"F0.wireOp",EDGE,"E25.6"),sQuery(id+"F0.wireOp",EDGE,"E25.7")])],"isStart":false});
            extrude(context, id + "F17", {"entities" : qUnion([Q0, Q1, Q2]), "operationType" : NewBodyOperationType.ADD, "endBound" : BoundingType.UP_TO_SURFACE, "depth" : 25 * mm, "endBoundEntityFace" : qUnion([Q3]), "offsetDistance" : 25 * mm});
        }
    });
